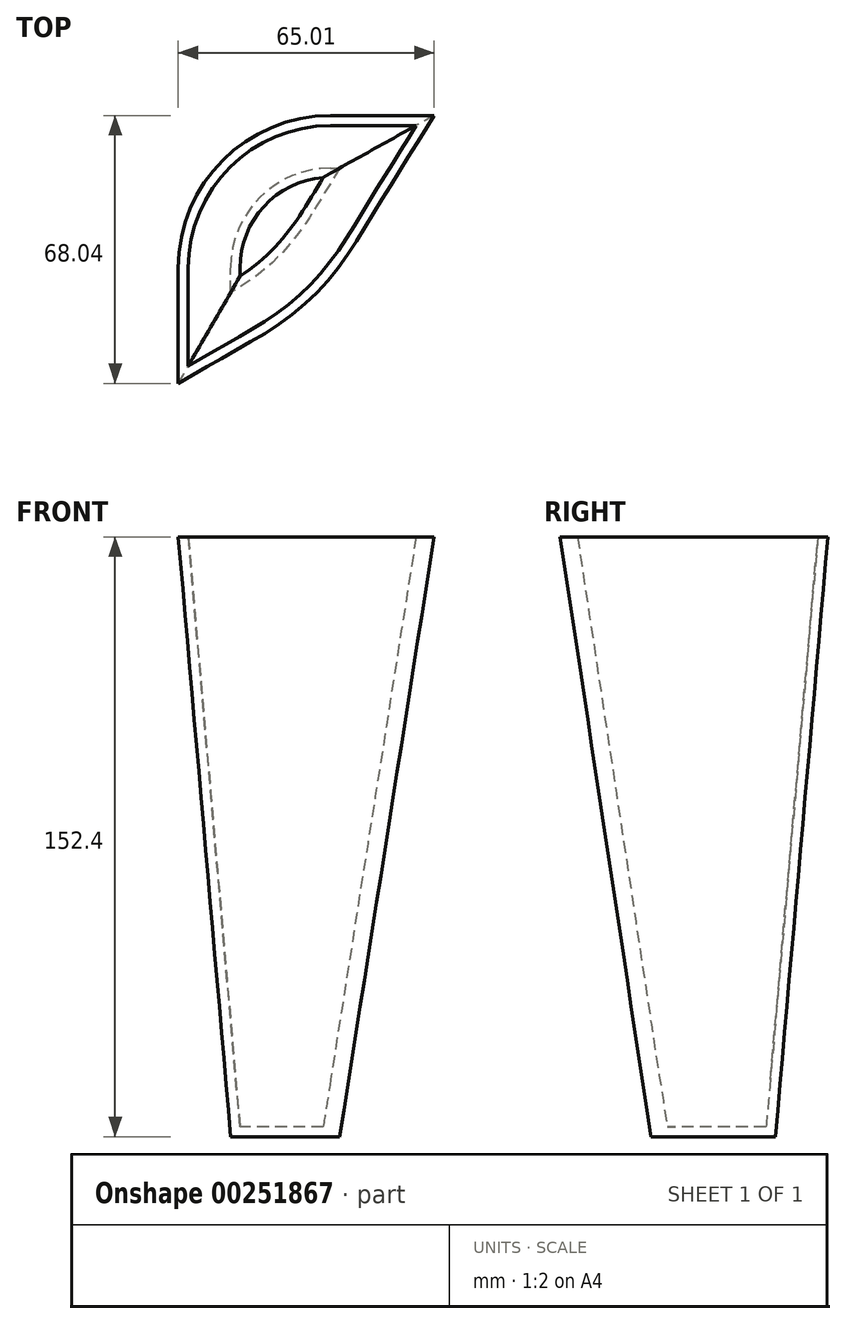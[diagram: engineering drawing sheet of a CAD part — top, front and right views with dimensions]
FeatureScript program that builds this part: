
annotation { "Feature Type Name" : "Feature", "Feature Type Description" : "" }
export const myFeature = defineFeature(function(context is Context, id is Id, definition is map)
    precondition{}
    {
        {
            var Q0;
            Q0=qCreatedBy(makeId("Top.planeOp"),FACE);
            var sketch = newSketch(context, id + "F0", { "sketchPlane" : qUnion([Q0])});
            skLineSegment(sketch, "E0.bottom", {"start": v(-33.35, 44.25) * mm, "end": v(-31.07, 44.25) * mm});
            skLineSegment(sketch, "E0.left", {"start": v(-58.75, 18.85) * mm, "end": v(-58.75, 12.61) * mm});
            skLineSegment(sketch, "E0.right", {"start": v(93.65, -20.38) * mm, "end": v(93.65, -31.95) * mm});
            skPoint(sketch, "E1.visualSharp", {"position": v(-58.75, 44.25) * mm});
            skArc(sketch, "E1.filletArc", {"start": v(-33.35, 44.25) * mm, "mid": v(-51.3, 36.81) * mm, "end": v(-58.75, 18.85) * mm});
            skPoint(sketch, "E2.visualSharp", {"position": v(93.65, 44.25) * mm});
            skPoint(sketch, "E3.visualSharp", {"position": v(93.65, -57.35) * mm});
            skArc(sketch, "E3.filletArc", {"start": v(68.25, -57.35) * mm, "mid": v(86.21, -49.91) * mm, "end": v(93.65, -31.95) * mm});
            skPoint(sketch, "E4.visualSharp", {"position": v(-58.75, -57.35) * mm});
            skFitSpline(sketch, "E5", {"points": [v(-67.44, 8.13) * mm, v(-77.47, 0) * mm, v(-69.8, -17.24) * mm, v(-32.93, -37.6) * mm, v(13.38, -67.1) * mm, v(101.88, -3.38) * mm, v(68.25, 29.07) * mm, v(46.72, 55.03) * mm, v(11.9, 52.08) * mm, v(-17.89, 58.28) * mm, v(-42.96, 25.83) * mm, v(-67.44, 8.13) * mm]});
            skPoint(sketch, "E2.filletArc.center.orphan", {"position": v(68.25, 18.85) * mm});
            skLineSegment(sketch, "E6.trimOffspring", {"start": v(45.55, -57.35) * mm, "end": v(68.25, -57.35) * mm});
            skSolve(sketch);
        }
        {
            var Q0;
            Q0=makeQuery(id+"F0.imprint","IMPRINT",FACE,{"disambiguationData":[TD([[makeQuery(id+"F0.imprint","IMPRINT",EDGE,{"derivedFrom":sQuery(id+"F0.wireOp",EDGE,"E0.bottom")}),-1.0]])]});
            extrude(context, id + "F1", {"entities" : qUnion([Q0]), "depth" : 152.4 * mm, "hasDraft" : true, "draftAngle" : 5 * degree});
        }
        {
            var Q0;
            Q0=makeQuery(id+"F1.opExtrude","CAP_FACE",FACE,{"disambiguationData":[OSD([sQuery(id+"F0.wireOp",EDGE,"E0.bottom"),sQuery(id+"F0.wireOp",EDGE,"E0.left"),sQuery(id+"F0.wireOp",EDGE,"E0.right"),sQuery(id+"F0.wireOp",EDGE,"E1.filletArc"),sQuery(id+"F0.wireOp",EDGE,"E3.filletArc"),sQuery(id+"F0.wireOp",EDGE,"E5"),sQuery(id+"F0.wireOp",EDGE,"E5"),sQuery(id+"F0.wireOp",EDGE,"E6.trimOffspring")])],"isStart":false});
            shell(context, id + "F2", {"entities" : qUnion([Q0]), "thickness" : 2.54 * mm});
        }
    });
